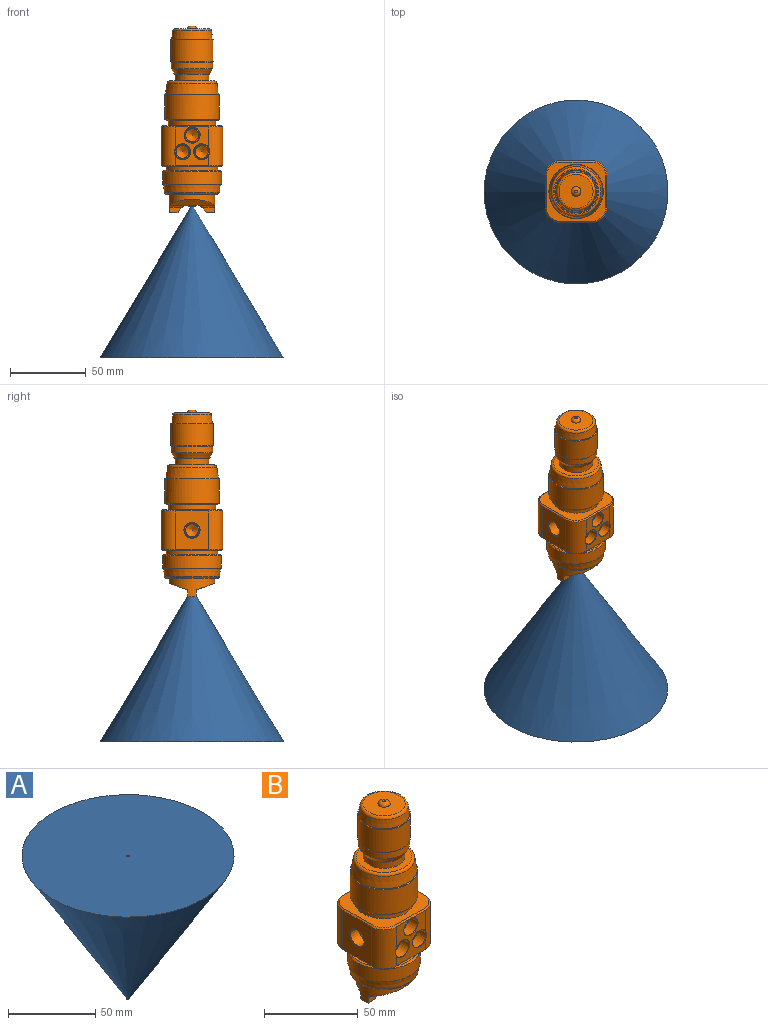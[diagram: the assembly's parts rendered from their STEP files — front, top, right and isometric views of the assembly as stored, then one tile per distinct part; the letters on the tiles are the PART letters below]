
ASSEMBLY  parts=2 mates=1
PART A: 3 faces, bbox 121.3x121.3x100 mm
  f0: cone r=60.65mm half-angle=31deg, axis (0,0,1), area 22458.5mm2, adj f1,f2
  f1: cylinder r=0.65mm len=100mm, axis (0,0,-1), area 408.4mm2, adj f0,f2
  f2: plane 121.3x121.3mm, normal (0,0,1), area 11554.8mm2, adj f0,f1
PART B: 129 faces, bbox 40.9x40.9x123.5 mm
  f0: cone r=5.33mm half-angle=45deg, axis (-1,0,0), area 9.4mm2, adj f1,f70
  f1: cone r=5.13mm half-angle=1.7deg, axis (-1,0,0), area 199.4mm2, adj f0,f128
  f2: cylinder r=4.22mm len=8.43mm, axis (-1,0,0), area 13.2mm2, adj f3,f128
  f3: cone r=4.22mm half-angle=59deg, axis (-1,0,0), area 65.2mm2, adj f2
  f4: cone r=5.33mm half-angle=45deg, axis (1,0,0), area 9.4mm2, adj f5,f74
  f5: cone r=5.13mm half-angle=1.7deg, axis (1,0,0), area 199.4mm2, adj f4,f127
  f6: cylinder r=4.22mm len=8.43mm, axis (1,0,0), area 13.2mm2, adj f7,f127
  f7: cone r=4.22mm half-angle=59deg, axis (1,0,0), area 65.2mm2, adj f6
  f8: cone r=5.33mm half-angle=45deg, axis (0,-1,0), area 9.3mm2, adj f9,f72,f73
  f9: cone r=5.13mm half-angle=1.7deg, axis (0,-1,0), area 199.4mm2, adj f8,f126
  f10: cylinder r=4.22mm len=8.43mm, axis (0,-1,0), area 13.2mm2, adj f11,f126
  f11: cone r=4.22mm half-angle=59deg, axis (0,-1,0), area 65.2mm2, adj f10
  f12: cone r=5.33mm half-angle=45deg, axis (0,-1,0), area 9.3mm2, adj f13,f71,f72
  f13: cone r=5.13mm half-angle=1.7deg, axis (0,-1,0), area 199.4mm2, adj f12,f125
  f14: cylinder r=4.22mm len=8.43mm, axis (0,-1,0), area 13.2mm2, adj f15,f125
  f15: cone r=4.22mm half-angle=59deg, axis (0,-1,0), area 65.2mm2, adj f14
  f16: cone r=5.33mm half-angle=45deg, axis (0,-1,0), area 9.4mm2, adj f17,f72
  f17: cone r=5.13mm half-angle=1.7deg, axis (0,-1,0), area 199.4mm2, adj f16,f124
  f18: cylinder r=4.22mm len=8.43mm, axis (0,-1,0), area 13.2mm2, adj f19,f124
  f19: cone r=4.22mm half-angle=59deg, axis (0,-1,0), area 65.2mm2, adj f18
  f20: cylinder r=0.38mm len=5.2mm, axis (0.8,0,-0.6), area 13.9mm2, adj f53,f123
  f21: cylinder r=0.75mm len=5.7mm, axis (0.8,0,-0.6), area 28.1mm2, adj f53,f122
  f22: cylinder r=0.38mm len=5.2mm, axis (-0.8,0,-0.6), area 13.9mm2, adj f56,f121
  f23: cylinder r=0.75mm len=5.7mm, axis (-0.8,0,-0.6), area 28.1mm2, adj f56,f120
  f24: cone r=3.4mm half-angle=59deg, axis (0,1,0), area 42.4mm2, adj f52,f111,f112,f118
  f25: torus R=14.88mm, axis (0,0,1), area 224.6mm2, adj f37,f81
  f26: torus R=11.24mm, axis (0,0,1), area 176.1mm2, adj f42,f77
  f27: torus R=16.67mm, axis (0,0,-1), area 253mm2, adj f46,f64
  f28: cone r=19.13mm half-angle=45deg, axis (0,0,1), area 56.6mm2, adj f45,f65
  f29: cone r=17.93mm half-angle=45deg, axis (0,0,-1), area 52.1mm2, adj f36,f82
  f30: cone r=14.1mm half-angle=45deg, axis (0,0,-1), area 40.9mm2, adj f41,f78
  f31: cone r=13.77mm half-angle=45deg, axis (0,0,1), area 40.9mm2, adj f41,f79
  f32: cone r=19.46mm half-angle=45deg, axis (0,0,-1), area 134.5mm2, adj f45,f66
  f33: cone r=17.14mm half-angle=45deg, axis (0,0,1), area 123.7mm2, adj f36,f83
  f34: cone r=1.96mm half-angle=45deg, axis (0,0,1), area 16.6mm2, adj f55,f63
  f35: cylinder r=15.63mm len=31.27mm, axis (0,0,-1), area 338.7mm2, adj f83,f84
  f36: cylinder r=17.93mm len=35.86mm, axis (0,0,-1), area 1833.4mm2, adj f29,f33
  f37: cone r=17.55mm half-angle=8.5deg, axis (0,0,-1), area 797.3mm2, adj f25,f82
  f38: cylinder r=11.11mm len=22.22mm, axis (0,0,-1), area 299.6mm2, adj f80,f81
  f39: cone r=11.5mm half-angle=30.8deg, axis (0,0,1), area 331.1mm2, adj f40,f80
  f40: cylinder r=13.64mm len=27.28mm, axis (0,0,-1), area 374.4mm2, adj f39,f79
  f41: cylinder r=14.1mm len=28.2mm, axis (0,0,-1), area 1306.2mm2, adj f30,f31
  f42: cone r=13.49mm half-angle=7.1deg, axis (0,0,-1), area 445.8mm2, adj f26,f78
  f43: torus R=0.92mm, axis (0,0,-1), area 45.9mm2, adj f76,f77
  f44: cylinder r=17.17mm len=34.33mm, axis (0,0,-1), area 264.5mm2, adj f66,f67
  f45: cylinder r=19.46mm len=38.93mm, axis (0,0,-1), area 1006mm2, adj f28,f32
  f46: cone r=18.06mm half-angle=7.5deg, axis (0,0,1), area 596.3mm2, adj f27,f65
  f47: cylinder r=1.75mm len=6.35mm, axis (0,0,-1), area 69.8mm2, adj f62,f63
  f48: cylinder r=1.05mm len=6.35mm, axis (0,0,-1), area 41.9mm2, adj f61,f62
  f49: cylinder r=0.35mm len=25.4mm, axis (0,0,-1), area 55.9mm2, adj f60,f61
  f50: torus R=5.52mm, axis (0,0,-1), area 11.7mm2, adj f53,f55,f101,f105,f108,f109
  f51: cylinder r=15.02mm len=30.04mm, axis (0,0,-1), area 540.3mm2, adj f57,f59,f64,f101,f102,f103,f104,f105
  f52: cylinder r=3.4mm len=8.9mm, axis (0,1,0), area 64.4mm2, adj f24,f54,f114,f116
  f53: cone r=6.35mm half-angle=35deg, axis (0,0,-1), area 26.8mm2, adj f20,f21,f50,f59,f104,f105,f109,f110
  f54: plane 21.59x5.49mm, normal (0,1,0), area 110.1mm2, adj f52,f69,f75,f85,f114,f115,f116,f119
  f55: plane 11.05x7.81mm, normal (0,0,-1), area 54.7mm2, adj f34,f50,f58,f101,f108
  f56: cone r=6.35mm half-angle=35deg, axis (0,0,-1), area 26.8mm2, adj f22,f23,f57,f58,f102,f103,f106,f107
  f57: plane 5.75x5.58mm, normal (0,0,-1), area 30.1mm2, adj f51,f56,f103,f106
  f58: torus R=5.52mm, axis (0,0,-1), area 11.7mm2, adj f55,f56,f101,f102,f107,f108
  f59: plane 5.75x5.58mm, normal (0,0,-1), area 30.1mm2, adj f51,f53,f104,f110
  f60: plane 0.7x0.7mm, normal (0,0,-1), area 0.4mm2, adj f49
  f61: plane 2.1x2.1mm, normal (0,0,-1), area 3.1mm2, adj f48,f49
  f62: plane 3.5x3.5mm, normal (0,0,-1), area 6.2mm2, adj f47,f48
  f63: plane 3.91x3.91mm, normal (0,0,-1), area 2.4mm2, adj f34,f47
  f64: plane 33.33x33.33mm, normal (0,0,-1), area 163.8mm2, adj f27,f51
  f65: plane 38.27x38.27mm, normal (0,0,-1), area 26.9mm2, adj f28,f46
  f66: plane 37.34x37.34mm, normal (0,0,1), area 169.5mm2, adj f32,f44
  f67: plane 39.05x39.05mm, normal (0,0,-1), area 533.9mm2, adj f44,f93,f94,f95,f96,f97,f98,f99
  f68: plane 21.59x16.77mm, normal (0,1,0), area 353.6mm2, adj f69,f75,f93,f111,f113,f115,f117,f119
  f69: cylinder r=9.53mm len=25.46mm, axis (0,0,1), area 378mm2, adj f54,f68,f70,f86,f94,f119
  f70: plane 25.46x21.59mm, normal (-1,0,0), area 460.4mm2, adj f0,f69,f71,f88,f96
  f71: cylinder r=9.53mm len=25.46mm, axis (0,0,1), area 377.5mm2, adj f12,f70,f72,f90,f98
  f72: plane 25.46x21.59mm, normal (0,-1,0), area 288.7mm2, adj f8,f12,f16,f71,f73,f92,f100
  f73: cylinder r=9.53mm len=25.46mm, axis (0,0,1), area 377.6mm2, adj f8,f72,f74,f91,f99
  f74: plane 25.46x21.59mm, normal (1,0,0), area 460.4mm2, adj f4,f73,f75,f89,f97
  f75: cylinder r=9.53mm len=25.46mm, axis (0,0,1), area 377.9mm2, adj f54,f68,f74,f87,f95,f115
  f76: plane 1.84x1.84mm, normal (0,0,1), area 2.7mm2, adj f43
  f77: plane 22.49x22.49mm, normal (0,0,1), area 364.3mm2, adj f26,f43
  f78: plane 27.54x27.54mm, normal (0,0,1), area 24.2mm2, adj f30,f42
  f79: plane 27.54x27.54mm, normal (0,0,-1), area 11.2mm2, adj f31,f40
  f80: plane 22.99x22.99mm, normal (0,0,-1), area 27.2mm2, adj f38,f39
  f81: plane 29.76x29.76mm, normal (0,0,1), area 307.5mm2, adj f25,f38
  f82: plane 35.2x35.2mm, normal (0,0,1), area 5.8mm2, adj f29,f37
  f83: plane 34.28x34.28mm, normal (0,0,-1), area 155mm2, adj f33,f35
  f84: plane 39.05x39.05mm, normal (0,0,1), area 691.9mm2, adj f35,f85,f86,f87,f88,f89,f90,f91
  f85: plane 21.59x0.79mm, normal (0,0.71,0.71), area 24.2mm2, adj f54,f84,f86,f87
  f86: cone r=8.73mm half-angle=45deg, axis (0,0,-1), area 16.1mm2, adj f69,f84,f85,f88
  f87: cone r=8.73mm half-angle=45deg, axis (0,0,-1), area 16.1mm2, adj f75,f84,f85,f89
  f88: plane 21.59x0.79mm, normal (-0.71,0,0.71), area 24.2mm2, adj f70,f84,f86,f90
  f89: plane 21.59x0.79mm, normal (0.71,0,0.71), area 24.2mm2, adj f74,f84,f87,f91
  f90: cone r=8.73mm half-angle=45deg, axis (0,0,-1), area 16.1mm2, adj f71,f84,f88,f92
  f91: cone r=8.73mm half-angle=45deg, axis (0,0,-1), area 16.1mm2, adj f73,f84,f89,f92
  f92: plane 21.59x0.79mm, normal (0,-0.71,0.71), area 24.2mm2, adj f72,f84,f90,f91
  f93: plane 21.59x0.79mm, normal (0,0.71,-0.71), area 24.2mm2, adj f67,f68,f94,f95
  f94: cone r=9.53mm half-angle=45deg, axis (0,0,1), area 16.1mm2, adj f67,f69,f93,f96
  f95: cone r=9.53mm half-angle=45deg, axis (0,0,1), area 16.1mm2, adj f67,f75,f93,f97
  f96: plane 21.59x0.79mm, normal (-0.71,0,-0.71), area 24.2mm2, adj f67,f70,f94,f98
  f97: plane 21.59x0.79mm, normal (0.71,0,-0.71), area 24.2mm2, adj f67,f74,f95,f99
  f98: cone r=9.53mm half-angle=45deg, axis (0,0,1), area 16.1mm2, adj f67,f71,f96,f100
  f99: cone r=9.53mm half-angle=45deg, axis (0,0,1), area 16.1mm2, adj f67,f73,f97,f100
  f100: plane 21.59x0.79mm, normal (0,-0.71,-0.71), area 24.2mm2, adj f67,f72,f98,f99
  f101: plane 29.07x11.21mm, normal (0,0.34,-0.94), area 254.7mm2, adj f50,f51,f55,f58,f102,f105
  f102: cylinder r=1.59mm len=10.43mm, axis (-1,0,0), area 17.2mm2, adj f51,f56,f58,f101,f103
  f103: plane 8.19x3.55mm, normal (0,1,0), area 21.7mm2, adj f51,f56,f57,f102
  f104: plane 8.19x3.55mm, normal (0,1,0), area 21.7mm2, adj f51,f53,f59,f105
  f105: cylinder r=1.59mm len=10.43mm, axis (1,0,0), area 17.2mm2, adj f50,f51,f53,f101,f104
  f106: plane 8.19x3.55mm, normal (0,-1,0), area 21.7mm2, adj f51,f56,f57,f107
  f107: cylinder r=1.59mm len=10.43mm, axis (-1,0,0), area 17.2mm2, adj f51,f56,f58,f106,f108
  f108: plane 29.07x11.21mm, normal (0,-0.34,-0.94), area 254.7mm2, adj f50,f51,f55,f58,f107,f109
  f109: cylinder r=1.59mm len=10.43mm, axis (1,0,0), area 17.2mm2, adj f50,f51,f53,f108,f110
  f110: plane 8.19x3.55mm, normal (0,-1,0), area 21.7mm2, adj f51,f53,f59,f109
  f111: cylinder r=3.4mm len=8.9mm, axis (0,1,0), area 64.4mm2, adj f24,f68,f113,f117
  f112: plane 9.09x3.3mm, normal (0,1,0), area 27.9mm2, adj f24,f113,f114,f115
  f113: plane 8.9x7.44mm, normal (0,0,1), area 66.2mm2, adj f68,f111,f112,f115
  f114: plane 8.9x7.44mm, normal (0,0,-1), area 66.2mm2, adj f52,f54,f112,f115
  f115: cylinder r=1.65mm len=8.9mm, axis (0,1,0), area 46.2mm2, adj f54,f68,f75,f112,f113,f114
  f116: plane 8.9x7.44mm, normal (0,0,-1), area 66.2mm2, adj f52,f54,f118,f119
  f117: plane 8.9x7.44mm, normal (0,0,1), area 66.2mm2, adj f68,f111,f118,f119
  f118: plane 9.09x3.3mm, normal (0,1,0), area 27.9mm2, adj f24,f116,f117,f119
  f119: cylinder r=1.65mm len=8.9mm, axis (0,1,0), area 46.2mm2, adj f54,f68,f69,f116,f117,f118
  f120: plane 1.5x1.2mm, normal (-0.8,0,-0.6), area 1.8mm2, adj f23
  f121: plane 0.75x0.6mm, normal (-0.8,0,-0.6), area 0.4mm2, adj f22
  f122: plane 1.5x1.2mm, normal (0.8,0,-0.6), area 1.8mm2, adj f21
  f123: plane 0.75x0.6mm, normal (0.8,0,-0.6), area 0.4mm2, adj f20
  f124: plane 9.88x9.88mm, normal (0,-1,0), area 20.9mm2, adj f17,f18
  f125: plane 9.88x9.88mm, normal (0,-1,0), area 20.9mm2, adj f13,f14
  f126: plane 9.88x9.88mm, normal (0,-1,0), area 20.9mm2, adj f9,f10
  f127: plane 9.88x9.88mm, normal (1,0,0), area 20.9mm2, adj f5,f6
  f128: plane 9.88x9.88mm, normal (-1,0,0), area 20.9mm2, adj f1,f2
PLACE A rot(axis=(1,0,0),180deg) t=(-174.18,-2.01,-131.69)mm
PLACE B t=(-174.18,-2.01,-74.32)mm
MATE fastened A.f0 <-> B.f25  axis (0,0,1) through (-174.18,-2.01,-131.69)mm
